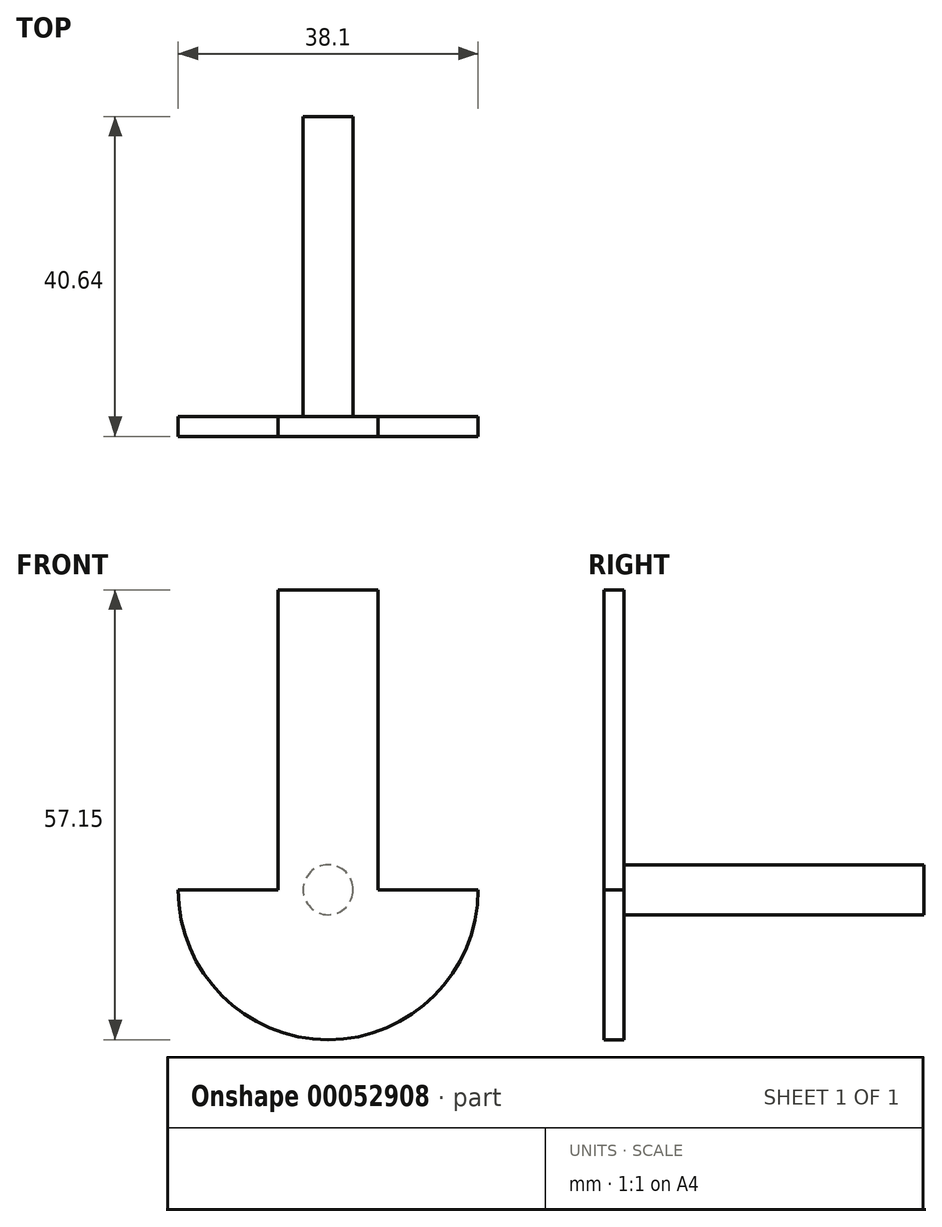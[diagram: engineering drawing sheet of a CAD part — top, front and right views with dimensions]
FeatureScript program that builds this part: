
annotation { "Feature Type Name" : "Feature", "Feature Type Description" : "" }
export const myFeature = defineFeature(function(context is Context, id is Id, definition is map)
    precondition{}
    {
        {
            var Q0;
            Q0=qCreatedBy(makeId("Front.planeOp"),FACE);
            var sketch = newSketch(context, id + "F0", { "sketchPlane" : qUnion([Q0])});
            skCircle(sketch, "E0", {"center": v(0, 0) * mm, "radius": 3.18 * mm});
            skSolve(sketch);
        }
        {
            var Q0;
            Q0 = qSketchRegion(id + "F0", true);
            extrude(context, id + "F1", {"entities" : qUnion([Q0]), "oppositeDirection" : true, "depth" : 38.1 * mm});
        }
        {
            var Q0;
            Q0=makeQuery(id+"F0.imprint","IMPRINT",FACE,{"disambiguationData":[TD([[makeQuery(id+"F0.imprint","IMPRINT",EDGE,{"derivedFrom":sQuery(id+"F0.wireOp",EDGE,"E0")}),1.0]])]});
            var sketch = newSketch(context, id + "F2", { "sketchPlane" : qUnion([Q0])});
            skArc(sketch, "E1", {"start": v(-19.05, 0) * mm, "mid": v(0, -19.05) * mm, "end": v(19.05, 0) * mm});
            skLineSegment(sketch, "E2", {"start": v(6.35, 0) * mm, "end": v(19.05, 0) * mm});
            skLineSegment(sketch, "E3", {"start": v(-6.35, 0) * mm, "end": v(-19.05, 0) * mm});
            skPoint(sketch, "E4.end.orphan", {"position": v(0, 39.02) * mm});
            skPoint(sketch, "E4.start.orphan", {"position": v(-32.13, 0) * mm});
            skLineSegment(sketch, "E5.left", {"start": v(-6.35, 38.1) * mm, "end": v(-6.35, 0) * mm});
            skLineSegment(sketch, "E5.right", {"start": v(6.35, 38.1) * mm, "end": v(6.35, 0) * mm});
            skLineSegment(sketch, "E6.0", {"start": v(-6.35, 38.1) * mm, "end": v(6.35, 38.1) * mm});
            skSolve(sketch);
        }
        {
            var Q0;
            Q0 = qSketchRegion(id + "F2", true);
            extrude(context, id + "F3", {"entities" : qUnion([Q0]), "operationType" : NewBodyOperationType.ADD, "depth" : 2.54 * mm});
        }
    });
